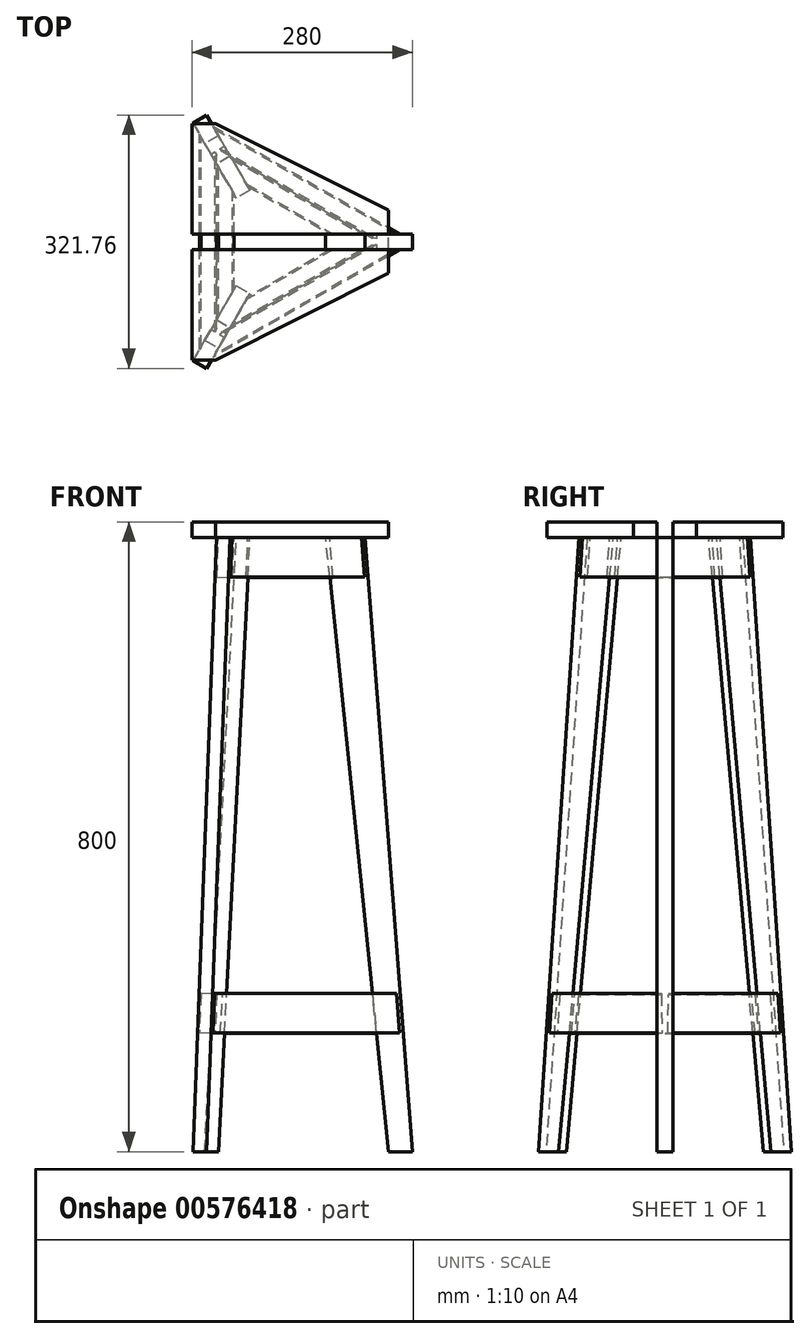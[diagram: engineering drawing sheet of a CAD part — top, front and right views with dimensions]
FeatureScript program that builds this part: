
annotation { "Feature Type Name" : "Feature", "Feature Type Description" : "" }
export const myFeature = defineFeature(function(context is Context, id is Id, definition is map)
    precondition{}
    {
        {
            var Q0;
            Q0=qCreatedBy(makeId("Front.planeOp"),FACE);
            var sketch = newSketch(context, id + "F0", { "sketchPlane" : qUnion([Q0])});
            skLineSegment(sketch, "E0", {"start": v(-100, 780) * mm, "end": v(150, 780) * mm});
            skLineSegment(sketch, "E1", {"start": v(120, 780) * mm, "end": v(180, 0) * mm});
            skLineSegment(sketch, "E2", {"start": v(164.62, 200) * mm, "end": v(0, 200) * mm});
            skPoint(sketch, "E3", {"position": v(0, 780) * mm});
            skLineSegment(sketch, "E4", {"start": v(-100, 780) * mm, "end": v(-100, 800) * mm});
            skLineSegment(sketch, "E5", {"start": v(-100, 800) * mm, "end": v(150, 800) * mm});
            skLineSegment(sketch, "E6", {"start": v(150, 800) * mm, "end": v(150, 780) * mm});
            skLineSegment(sketch, "E7", {"start": v(0, 780) * mm, "end": v(0, 0) * mm});
            skSolve(sketch);
        }
        {
            var Q0;
            Q0=qCreatedBy(makeId("Top.planeOp"),FACE);
            var Q1;
            Q1=sQuery(id+"F0.wireOp",VERTEX,"E5.start");
            cPlane(context, id + "F1", {"entities" : qUnion([Q0, Q1]), "cplaneType" : CPlaneType.PLANE_POINT, "offset" : 25 * mm, "width" : 150 * mm, "height" : 150 * mm});
        }
        {
            var Q0;
            Q0=qCreatedBy(id+"F1.planeOp",FACE);
            var sketch = newSketch(context, id + "F2", { "sketchPlane" : qUnion([Q0])});
            skLineSegment(sketch, "E8", {"start": v(150, -10) * mm, "end": v(-100, -10) * mm});
            skLineSegment(sketch, "E9", {"start": v(-100, -10) * mm, "end": v(-100, -150) * mm});
            skLineSegment(sketch, "E10", {"start": v(-100, -150) * mm, "end": v(-70, -150) * mm});
            skLineSegment(sketch, "E11", {"start": v(-70, -150) * mm, "end": v(150, -40) * mm});
            skLineSegment(sketch, "E12", {"start": v(150, -40) * mm, "end": v(150, -10) * mm});
            skSolve(sketch);
        }
        {
            var Q0;
            Q0=makeQuery(id+"F2.imprint","IMPRINT",FACE,{"disambiguationData":[TD([[makeQuery(id+"F2.imprint","IMPRINT",EDGE,{"derivedFrom":sQuery(id+"F2.wireOp",EDGE,"E8")}),1.0]])]});
            extrude(context, id + "F3", {"entities" : qUnion([Q0]), "oppositeDirection" : true, "depth" : 20 * mm, "offsetDistance" : 25 * mm});
        }
        {
            var Q0;
            Q0=qCreatedBy(makeId("Front.planeOp"),FACE);
            var sketch = newSketch(context, id + "F4", { "sketchPlane" : qUnion([Q0])});
            skLineSegment(sketch, "E13", {"start": v(70, 780) * mm, "end": v(120, 780) * mm});
            skLineSegment(sketch, "E14", {"start": v(120, 780) * mm, "end": v(180, 0) * mm});
            skLineSegment(sketch, "E15", {"start": v(180, 0) * mm, "end": v(150, 0) * mm});
            skLineSegment(sketch, "E16", {"start": v(150, 0) * mm, "end": v(70, 780) * mm});
            skSolve(sketch);
        }
        {
            var Q0;
            Q0=makeQuery(id+"F4.imprint","IMPRINT",FACE,{"disambiguationData":[TD([[makeQuery(id+"F4.imprint","IMPRINT",EDGE,{"derivedFrom":sQuery(id+"F4.wireOp",EDGE,"E13")}),-1.0]])]});
            extrude(context, id + "F5", {"entities" : qUnion([Q0]), "endBound" : BoundingType.SYMMETRIC, "depth" : 20 * mm, "offsetDistance" : 25 * mm});
        }
        {
            var Q0;
            Q0=makeQuery(id+"F5.opExtrude","SWEPT_BODY",BODY,{"disambiguationData":[OSD([sQuery(id+"F4.wireOp",EDGE,"E13"),sQuery(id+"F4.wireOp",EDGE,"E14"),sQuery(id+"F4.wireOp",EDGE,"E15"),sQuery(id+"F4.wireOp",EDGE,"E16")])]});
            var Q1;
            Q1=sQuery(id+"F0.wireOp",EDGE,"E7");
            circularPattern(context, id + "F6", {"entities" : qUnion([Q0]), "axis" : qUnion([Q1]), "angle" : 360 * degree, "instanceCount" : 3, "equalSpace" : true});
        }
        {
            var Q0;
            Q0=makeQuery(id+"F3.opExtrude","SWEPT_BODY",BODY,{"disambiguationData":[OSD([sQuery(id+"F2.wireOp",EDGE,"E8"),sQuery(id+"F2.wireOp",EDGE,"E9"),sQuery(id+"F2.wireOp",EDGE,"E10"),sQuery(id+"F2.wireOp",EDGE,"E11"),sQuery(id+"F2.wireOp",EDGE,"E12")])]});
            var Q1;
            Q1=qCreatedBy(makeId("Front.planeOp"),FACE);
            mirror(context, id + "F7", {"operationType" : NewBodyOperationType.ADD, "entities" : qUnion([Q0]), "mirrorPlane" : qUnion([Q1])});
        }
        {
            var Q0;
            Q0=qCreatedBy(makeId("Front.planeOp"),FACE);
            var sketch = newSketch(context, id + "F8", { "sketchPlane" : qUnion([Q0])});
            skLineSegment(sketch, "E17.bottom", {"start": v(-46.35, 779.23) * mm, "end": v(-66.33, 780) * mm});
            skLineSegment(sketch, "E17.top", {"start": v(-48.27, 729.27) * mm, "end": v(-68.26, 730.04) * mm});
            skLineSegment(sketch, "E17.left", {"start": v(-46.35, 779.23) * mm, "end": v(-48.27, 729.27) * mm});
            skLineSegment(sketch, "E17.right", {"start": v(-66.33, 780) * mm, "end": v(-68.26, 730.04) * mm});
            skPoint(sketch, "E17.middle", {"position": v(-57.3, 754.63) * mm});
            skLineSegment(sketch, "E18.bottom", {"start": v(-90.53, 150.8) * mm, "end": v(-70.55, 150.04) * mm});
            skLineSegment(sketch, "E18.top", {"start": v(-88.61, 200.77) * mm, "end": v(-68.63, 200) * mm});
            skLineSegment(sketch, "E18.left", {"start": v(-90.53, 150.8) * mm, "end": v(-88.61, 200.77) * mm});
            skLineSegment(sketch, "E18.right", {"start": v(-70.55, 150.04) * mm, "end": v(-68.63, 200) * mm});
            skPoint(sketch, "E18.middle", {"position": v(-79.58, 175.4) * mm});
            skLineSegment(sketch, "E19", {"start": v(-45, 754) * mm, "end": v(-69.61, 755.27) * mm});
            skSolve(sketch);
        }
        {
            var Q0;
            Q0=makeQuery(id+"F8.imprint","IMPRINT",FACE,{"disambiguationData":[TD([[makeQuery(id+"F8.imprint","IMPRINT",EDGE,{"derivedFrom":sQuery(id+"F8.wireOp",EDGE,"E18.bottom")}),1.0]])]});
            var Q1;
            {var subQ0=sQuery(id+"F8.wireOp",EDGE,"E17.top");Q1=makeQuery(id+"F8.imprint","IMPRINT",FACE,{"disambiguationData":[TD([[makeQuery(id+"F8.imprint","IMPRINT",EDGE,{"derivedFrom":subQ0}),-1.0]])]});}
            var Q2;
            {var subQ0=sQuery(id+"F8.wireOp",EDGE,"E17.bottom");Q2=makeQuery(id+"F8.imprint","IMPRINT",FACE,{"disambiguationData":[TD([[makeQuery(id+"F8.imprint","IMPRINT",EDGE,{"derivedFrom":subQ0}),1.0]])]});}
            extrude(context, id + "F9", {"entities" : qUnion([Q0, Q1, Q2]), "endBound" : BoundingType.UP_TO_NEXT, "depth" : 25 * mm, "offsetDistance" : 25 * mm, "hasSecondDirection" : true, "secondDirectionBound" : SecondDirectionBoundingType.UP_TO_NEXT, "secondDirectionOppositeDirection" : true, "secondDirectionDepth" : 25 * mm});
        }
        {
            var Q0;
            Q0=makeQuery(id+"F9.opExtrude","SWEPT_BODY",BODY,{"disambiguationData":[OSD([sQuery(id+"F8.wireOp",EDGE,"E17.bottom"),sQuery(id+"F8.wireOp",EDGE,"E17.top"),sQuery(id+"F8.wireOp",EDGE,"E17.left"),sQuery(id+"F8.wireOp",EDGE,"E17.right")])]});
            var Q1;
            Q1=makeQuery(id+"F9.opExtrude","SWEPT_BODY",BODY,{"disambiguationData":[OSD([sQuery(id+"F8.wireOp",EDGE,"E18.bottom"),sQuery(id+"F8.wireOp",EDGE,"E18.top"),sQuery(id+"F8.wireOp",EDGE,"E18.left"),sQuery(id+"F8.wireOp",EDGE,"E18.right")])]});
            var Q2;
            Q2=sQuery(id+"F0.wireOp",EDGE,"E7");
            circularPattern(context, id + "F10", {"entities" : qUnion([Q0, Q1]), "axis" : qUnion([Q2]), "angle" : 360 * degree, "instanceCount" : 3, "equalSpace" : true});
        }
    });
